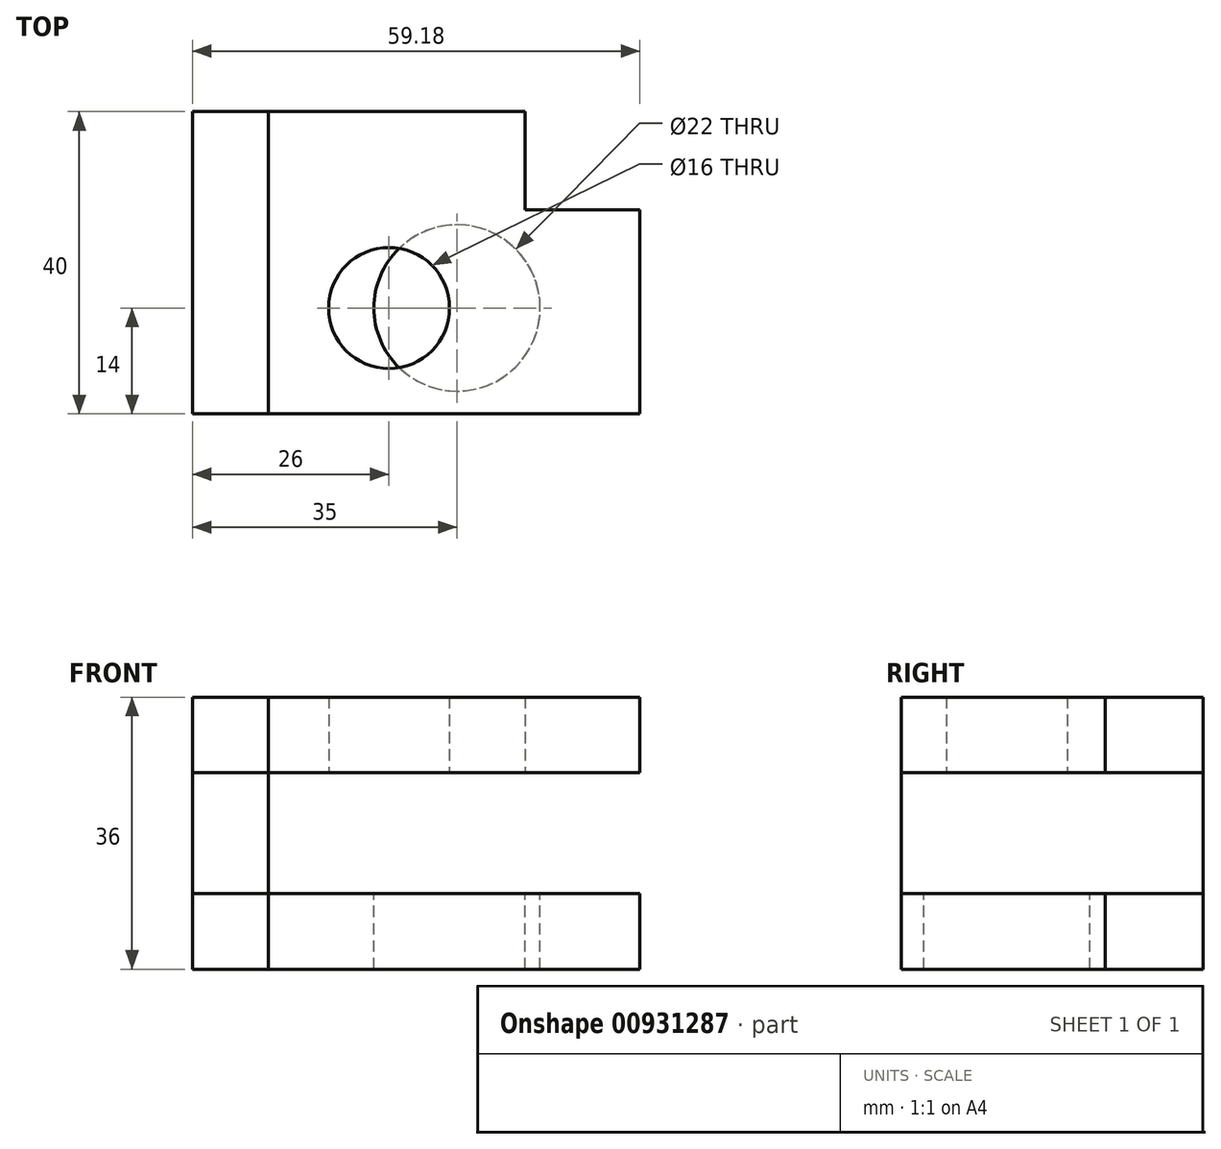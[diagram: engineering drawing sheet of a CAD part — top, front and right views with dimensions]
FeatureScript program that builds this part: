
annotation { "Feature Type Name" : "Feature", "Feature Type Description" : "" }
export const myFeature = defineFeature(function(context is Context, id is Id, definition is map)
    precondition{}
    {
        {
            var Q0;
            Q0=qCreatedBy(makeId("Top.planeOp"),FACE);
            var sketch = newSketch(context, id + "F0", { "sketchPlane" : qUnion([Q0])});
            skLineSegment(sketch, "E0.bottom", {"start": v(-17, 20) * mm, "end": v(17, 20) * mm});
            skLineSegment(sketch, "E0.top", {"start": v(-17, -20) * mm, "end": v(17, -20) * mm});
            skLineSegment(sketch, "E0.left", {"start": v(-17, 20) * mm, "end": v(-17, -20) * mm});
            skLineSegment(sketch, "E0.right", {"start": v(17, 20) * mm, "end": v(17, -20) * mm});
            skPoint(sketch, "E0.middle", {"position": v(0, 0) * mm});
            skLineSegment(sketch, "E1", {"start": v(-17, 14.75) * mm, "end": v(-1, 14.75) * mm, "construction": true});
            skLineSegment(sketch, "E2", {"start": v(-1, 20) * mm, "end": v(-1, -6) * mm, "construction": true});
            skCircle(sketch, "E3", {"center": v(-1, -6) * mm, "radius": 8 * mm});
            skLineSegment(sketch, "E4", {"start": v(14.15, 20) * mm, "end": v(14.15, 7) * mm, "construction": true});
            skLineSegment(sketch, "E5.bottom", {"start": v(17, 7) * mm, "end": v(32.18, 7) * mm});
            skLineSegment(sketch, "E5.top", {"start": v(17, -20) * mm, "end": v(32.18, -20) * mm});
            skLineSegment(sketch, "E5.left", {"start": v(17, 7) * mm, "end": v(17, -20) * mm});
            skLineSegment(sketch, "E5.right", {"start": v(32.18, 7) * mm, "end": v(32.18, -20) * mm});
            skLineSegment(sketch, "E6.bottom", {"start": v(-17, -20) * mm, "end": v(-27, -20) * mm});
            skLineSegment(sketch, "E6.top", {"start": v(-17, 20) * mm, "end": v(-27, 20) * mm});
            skLineSegment(sketch, "E6.left", {"start": v(-17, -20) * mm, "end": v(-17, 20) * mm});
            skLineSegment(sketch, "E6.right", {"start": v(-27, -20) * mm, "end": v(-27, 20) * mm});
            skSolve(sketch);
        }
        {
            var Q0;
            Q0=makeQuery(id+"F0.imprint","IMPRINT",FACE,{"disambiguationData":[TD([[makeQuery(id+"F0.imprint","IMPRINT",EDGE,{"derivedFrom":sQuery(id+"F0.wireOp",EDGE,"E0.bottom")}),-1.0]])]});
            var Q1;
            Q1=makeQuery(id+"F0.imprint","IMPRINT",FACE,{"disambiguationData":[TD([[makeQuery(id+"F0.imprint","IMPRINT",EDGE,{"derivedFrom":sQuery(id+"F0.wireOp",EDGE,"E5.bottom")}),-1.0]])]});
            extrude(context, id + "F1", {"entities" : qUnion([Q0, Q1]), "depth" : 10 * mm, "offsetDistance" : 25 * mm});
        }
        {
            var Q0;
            Q0=makeQuery(id+"F0.imprint","IMPRINT",FACE,{"disambiguationData":[TD([[makeQuery(id+"F0.imprint","IMPRINT",EDGE,{"derivedFrom":sQuery(id+"F0.wireOp",EDGE,"E6.bottom")}),-1.0]])]});
            extrude(context, id + "F2", {"entities" : qUnion([Q0]), "depth" : -16 * mm, "offsetDistance" : 25 * mm});
        }
        {
            var Q0;
            Q0=makeQuery(id+"F0.imprint","IMPRINT",FACE,{"disambiguationData":[TD([[makeQuery(id+"F0.imprint","IMPRINT",EDGE,{"derivedFrom":sQuery(id+"F0.wireOp",EDGE,"E6.bottom")}),-1.0]])]});
            extrude(context, id + "F3", {"entities" : qUnion([Q0]), "depth" : 10 * mm, "offsetDistance" : 25 * mm});
        }
        {
            var Q0;
            Q0=makeQuery(id+"F2.opExtrude","CAP_FACE",FACE,{"disambiguationData":[OSD([sQuery(id+"F0.wireOp",EDGE,"E6.bottom"),sQuery(id+"F0.wireOp",EDGE,"E6.top"),sQuery(id+"F0.wireOp",EDGE,"E6.left"),sQuery(id+"F0.wireOp",EDGE,"E6.right")])],"isStart":false});
            var sketch = newSketch(context, id + "F4", { "sketchPlane" : qUnion([Q0])});
            skLineSegment(sketch, "E7.bottom", {"start": v(-17, -20) * mm, "end": v(17, -20) * mm});
            skPoint(sketch, "E7.middle", {"position": v(-1.38, -0.2) * mm});
            skLineSegment(sketch, "E8.MirrorCS", {"start": v(-22, 20) * mm, "end": v(-22, -20) * mm});
            skLineSegment(sketch, "E9.MirrorCS", {"start": v(-22, -20) * mm, "end": v(-27, -20) * mm});
            skLineSegment(sketch, "E10.MirrorCS", {"start": v(-17, 20) * mm, "end": v(-17, -20) * mm});
            skLineSegment(sketch, "E11.MirrorCS", {"start": v(-17, 20) * mm, "end": v(-22, 20) * mm});
            skLineSegment(sketch, "E12.MirrorCS", {"start": v(-17, 20) * mm, "end": v(17, 20) * mm});
            skLineSegment(sketch, "E13.MirrorCS", {"start": v(17, -20) * mm, "end": v(17, 20) * mm});
            skLineSegment(sketch, "E14.MirrorCS", {"start": v(32.18, -7) * mm, "end": v(32.18, 20) * mm});
            skLineSegment(sketch, "E15.MirrorCS", {"start": v(17, 20) * mm, "end": v(32.18, 20) * mm});
            skLineSegment(sketch, "E16.MirrorCS", {"start": v(17, -7) * mm, "end": v(32.18, -7) * mm});
            skCircle(sketch, "E17.MirrorC", {"center": v(8, 6) * mm, "radius": 11 * mm});
            skLineSegment(sketch, "E18.MirrorCS", {"start": v(-1, -20) * mm, "end": v(-1, 6) * mm, "construction": true});
            skLineSegment(sketch, "E19.MirrorCS", {"start": v(-17, -14.75) * mm, "end": v(-1, -14.75) * mm, "construction": true});
            skLineSegment(sketch, "E20.MirrorCS", {"start": v(14.15, -20) * mm, "end": v(14.15, -7) * mm, "construction": true});
            skLineSegment(sketch, "E21", {"start": v(8, 6) * mm, "end": v(-22, 6) * mm, "construction": true});
            skSolve(sketch);
        }
        {
            var Q0;
            Q0 = qSketchRegion(id + "F4", true);
            extrude(context, id + "F5", {"entities" : qUnion([Q0]), "operationType" : NewBodyOperationType.ADD, "depth" : 10 * mm, "offsetDistance" : 25 * mm});
        }
        {
            var Q0;
            {var subQ0=sQuery(id+"F4.wireOp",EDGE,"E8.MirrorCS");Q0=makeQuery(id+"F4.imprint","IMPRINT",FACE,{"disambiguationData":[TD([[makeQuery(id+"F4.imprint","IMPRINT",EDGE,{"derivedFrom":subQ0}),1.0]])]});}
            var Q1;
            {var subQ0=sQuery(id+"F4.wireOp",EDGE,"E8.MirrorCS");Q1=makeQuery(id+"F4.imprint","IMPRINT",FACE,{"disambiguationData":[TD([[makeQuery(id+"F4.imprint","IMPRINT",EDGE,{"derivedFrom":subQ0}),-1.0]])]});}
            extrude(context, id + "F6", {"entities" : qUnion([Q0, Q1]), "depth" : 10 * mm, "offsetDistance" : 25 * mm});
        }
    });
